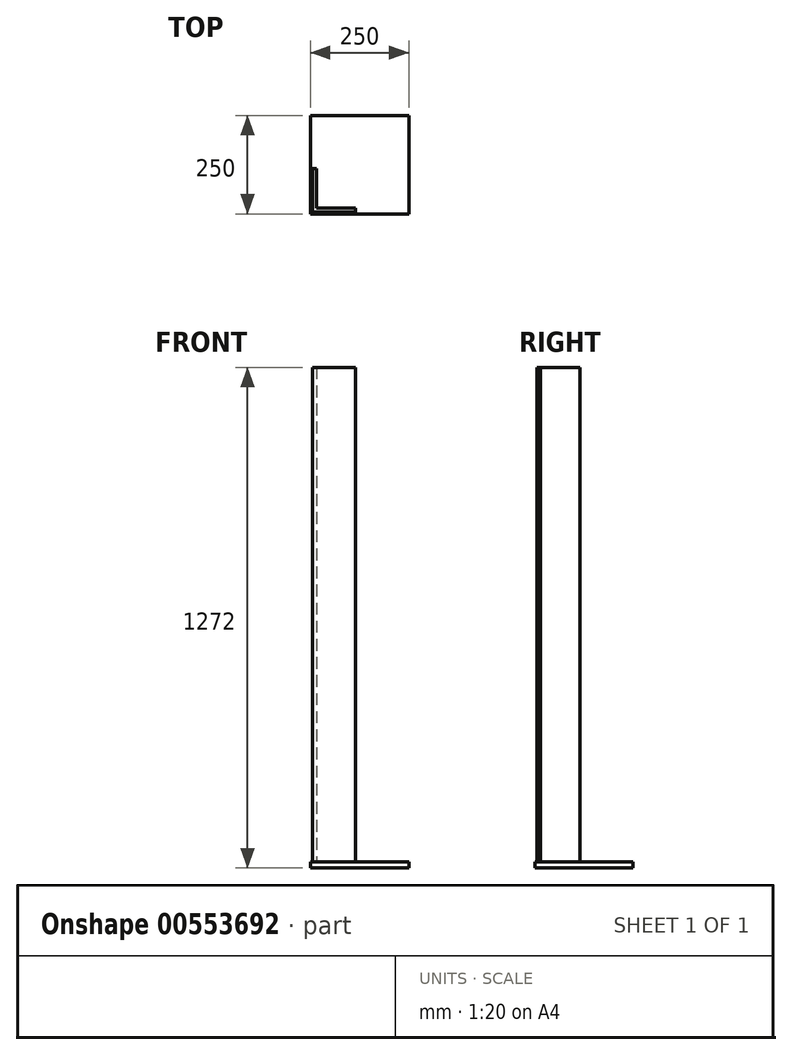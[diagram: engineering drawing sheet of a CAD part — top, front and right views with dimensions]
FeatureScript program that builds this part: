
annotation { "Feature Type Name" : "Feature", "Feature Type Description" : "" }
export const myFeature = defineFeature(function(context is Context, id is Id, definition is map)
    precondition{}
    {
        {
            var Q0;
            Q0=qCreatedBy(makeId("Top.planeOp"),FACE);
            var sketch = newSketch(context, id + "F0", { "sketchPlane" : qUnion([Q0])});
            skLineSegment(sketch, "E0.bottom", {"start": v(-125, 125) * mm, "end": v(125, 125) * mm});
            skLineSegment(sketch, "E0.top", {"start": v(-125, -125) * mm, "end": v(125, -125) * mm});
            skLineSegment(sketch, "E0.left", {"start": v(-125, 125) * mm, "end": v(-125, -125) * mm});
            skLineSegment(sketch, "E0.right", {"start": v(125, 125) * mm, "end": v(125, -125) * mm});
            skPoint(sketch, "E0.middle", {"position": v(0, 0) * mm});
            skSolve(sketch);
        }
        {
            var Q0;
            Q0=makeQuery(id+"F0.imprint","IMPRINT",FACE,{"disambiguationData":[TD([[makeQuery(id+"F0.imprint","IMPRINT",EDGE,{"derivedFrom":sQuery(id+"F0.wireOp",EDGE,"E0.bottom")}),-1.0]])]});
            extrude(context, id + "F1", {"entities" : qUnion([Q0]), "depth" : 15 * mm, "offsetDistance" : 25 * mm});
        }
        {
            var Q0;
            Q0=makeQuery(id+"F1.opExtrude","CAP_FACE",FACE,{"disambiguationData":[OSD([sQuery(id+"F0.wireOp",EDGE,"E0.bottom"),sQuery(id+"F0.wireOp",EDGE,"E0.top"),sQuery(id+"F0.wireOp",EDGE,"E0.left"),sQuery(id+"F0.wireOp",EDGE,"E0.right")])],"isStart":false});
            var sketch = newSketch(context, id + "F2", { "sketchPlane" : qUnion([Q0])});
            skLineSegment(sketch, "E1.bottom", {"start": v(-120, -10) * mm, "end": v(-110, -10) * mm});
            skLineSegment(sketch, "E1.top", {"start": v(-120, -120) * mm, "end": v(-110, -120) * mm});
            skLineSegment(sketch, "E1.left", {"start": v(-120, -10) * mm, "end": v(-120, -120) * mm});
            skLineSegment(sketch, "E1.right", {"start": v(-110, -10) * mm, "end": v(-110, -110) * mm});
            skLineSegment(sketch, "E2.bottom", {"start": v(-120, -120) * mm, "end": v(-10, -120) * mm});
            skLineSegment(sketch, "E2.top", {"start": v(-110, -110) * mm, "end": v(-10, -110) * mm});
            skLineSegment(sketch, "E2.left", {"start": v(-120, -120) * mm, "end": v(-120, -110) * mm});
            skLineSegment(sketch, "E2.right", {"start": v(-10, -120) * mm, "end": v(-10, -110) * mm});
            skSolve(sketch);
        }
        {
            var Q0;
            Q0=makeQuery(id+"F2.imprint","IMPRINT",FACE,{"disambiguationData":[TD([[makeQuery(id+"F2.imprint","IMPRINT",EDGE,{"derivedFrom":sQuery(id+"F2.wireOp",EDGE,"E1.bottom")}),-1.0]])]});
            extrude(context, id + "F3", {"entities" : qUnion([Q0]), "operationType" : NewBodyOperationType.ADD, "depth" : 1257 * mm, "offsetDistance" : 25 * mm});
        }
    });
